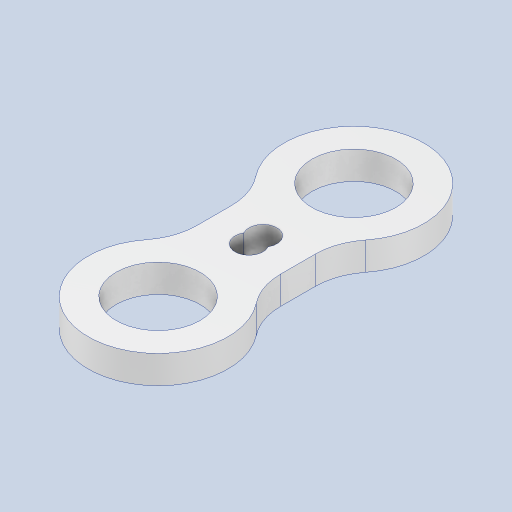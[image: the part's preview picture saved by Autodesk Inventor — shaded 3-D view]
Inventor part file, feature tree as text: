
AUTODESK INVENTOR PART (.ipt)
format: ipt  version: 2024 (Build 280153000, 153)  size: 200,192 bytes
history: native  units: mm
features: extrude x1, sketch x1
ambient origin geometry x8: Origin, YZ Plane, XZ Plane, XY Plane, X Axis, Y Axis, Z Axis, Center Point
bodies: Body1 (feature_tree)
feature tree (2):
  extrude  "Extrusión8"  Depth=10.0mm
  sketch  "Boceto1"  dims[d3=10.0mm d6=0.0mm d29=30.0mm d35=10.0mm d36=10.0mm d37=5.0mm d38=2.5mm d39=10.0mm d40=0.0mm d16=1.0mm d17=1.0mm d18=1.0mm d19=0.15mm d20=0.25mm d21=0.375mm d22=14.3117mm d23=0.75mm d24=20.594885mm d25=0.0625mm d26=0.75mm d27=0.375mm]
